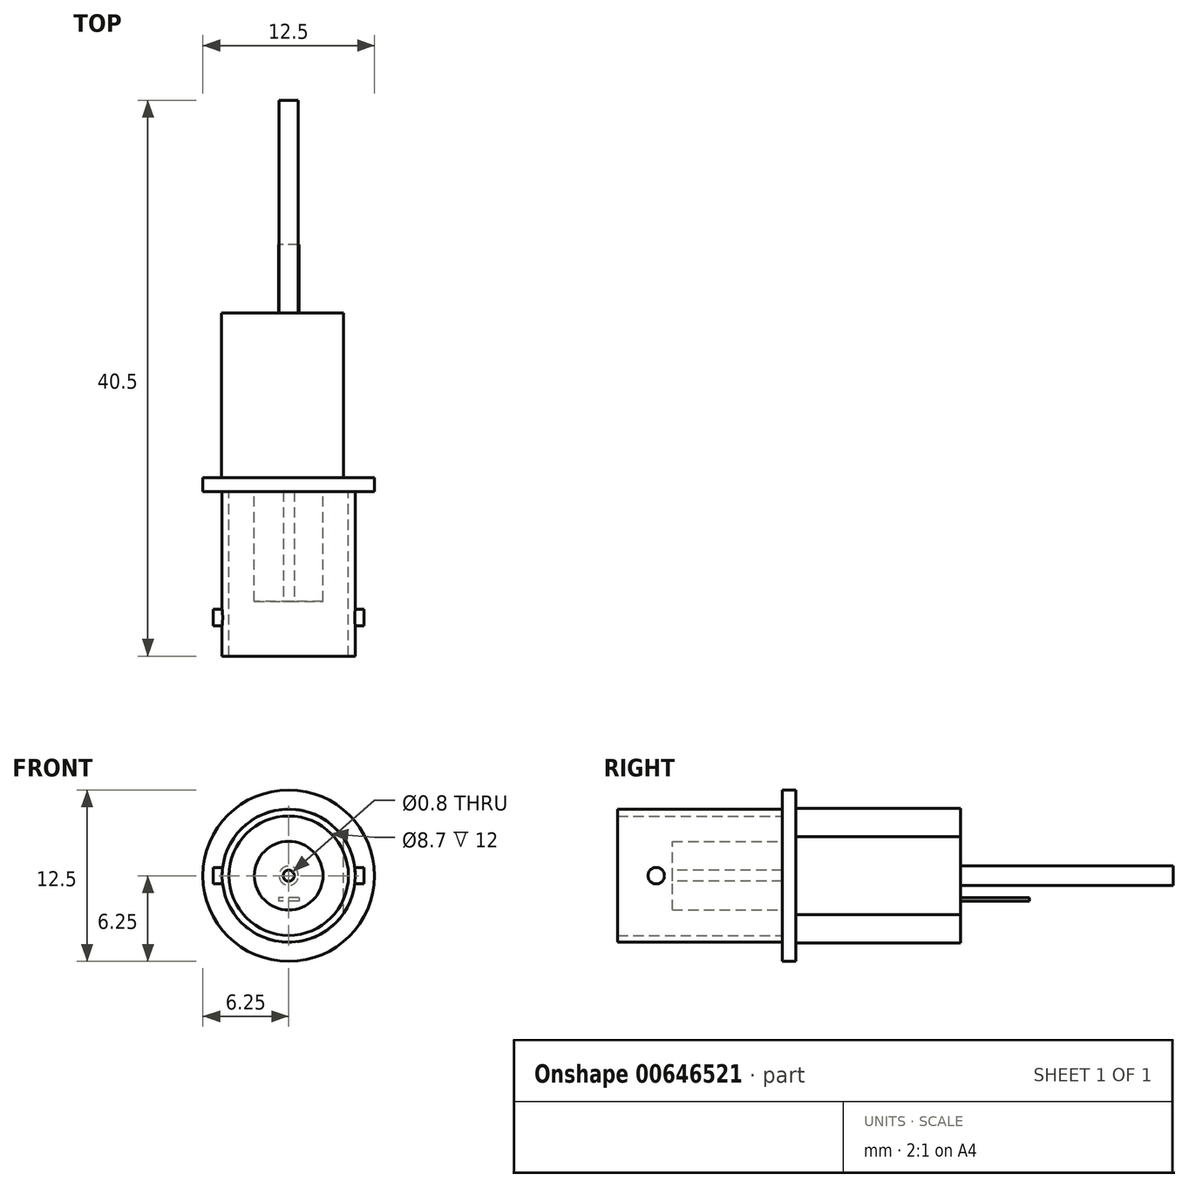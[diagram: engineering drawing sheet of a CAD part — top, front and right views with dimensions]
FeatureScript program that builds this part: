
annotation { "Feature Type Name" : "Feature", "Feature Type Description" : "" }
export const myFeature = defineFeature(function(context is Context, id is Id, definition is map)
    precondition{}
    {
        {
            var Q0;
            Q0=qCreatedBy(makeId("Front.planeOp"),FACE);
            var sketch = newSketch(context, id + "F0", { "sketchPlane" : qUnion([Q0])});
            skCircle(sketch, "E0", {"center": v(0, 0) * mm, "radius": 4.85 * mm});
            skCircle(sketch, "E1", {"center": v(0, 0) * mm, "radius": 4.35 * mm});
            skSolve(sketch);
        }
        {
            var Q0;
            Q0 = qSketchRegion(id + "F0", true);
            extrude(context, id + "F1", {"entities" : qUnion([Q0]), "depth" : 12 * mm, "offsetDistance" : 25 * mm});
        }
        {
            var Q0;
            Q0=qCreatedBy(makeId("Right.planeOp"),FACE);
            var sketch = newSketch(context, id + "F2", { "sketchPlane" : qUnion([Q0])});
            skCircle(sketch, "E2", {"center": v(-9.18, 0) * mm, "radius": 0.6 * mm});
            skSolve(sketch);
        }
        {
            var Q0;
            Q0 = qSketchRegion(id + "F2", true);
            extrude(context, id + "F3", {"entities" : qUnion([Q0]), "operationType" : NewBodyOperationType.ADD, "endBound" : BoundingType.SYMMETRIC, "depth" : 11 * mm, "offsetDistance" : 25 * mm});
        }
        {
            var Q0;
            Q0=qCreatedBy(makeId("Front.planeOp"),FACE);
            var sketch = newSketch(context, id + "F4", { "sketchPlane" : qUnion([Q0])});
            skCircle(sketch, "E3", {"center": v(0, 0) * mm, "radius": 4.35 * mm});
            skSolve(sketch);
        }
        {
            var Q0;
            Q0 = qSketchRegion(id + "F4", true);
            extrude(context, id + "F5", {"entities" : qUnion([Q0]), "operationType" : NewBodyOperationType.REMOVE, "depth" : 25 * mm, "offsetDistance" : 25 * mm});
        }
        {
            var Q0;
            Q0=qCreatedBy(makeId("Front.planeOp"),FACE);
            var sketch = newSketch(context, id + "F6", { "sketchPlane" : qUnion([Q0])});
            skCircle(sketch, "E4", {"center": v(0, 0) * mm, "radius": 2.5 * mm});
            skSolve(sketch);
        }
        {
            var Q0;
            Q0 = qSketchRegion(id + "F6", true);
            extrude(context, id + "F7", {"entities" : qUnion([Q0]), "depth" : 8 * mm, "offsetDistance" : 25 * mm});
        }
        {
            var Q0;
            Q0=makeQuery(id+"F7.opExtrude","CAP_FACE",FACE,{"disambiguationData":[OSD([sQuery(id+"F6.wireOp",EDGE,"E4")])],"isStart":false});
            var sketch = newSketch(context, id + "F8", { "sketchPlane" : qUnion([Q0])});
            skCircle(sketch, "E5", {"center": v(0, 0) * mm, "radius": 0.4 * mm});
            skSolve(sketch);
        }
        {
            var Q0;
            Q0 = qSketchRegion(id + "F8", true);
            extrude(context, id + "F9", {"entities" : qUnion([Q0]), "operationType" : NewBodyOperationType.REMOVE, "oppositeDirection" : true, "depth" : 25 * mm, "offsetDistance" : 25 * mm});
        }
        {
            var Q0;
            Q0=qCreatedBy(makeId("Front.planeOp"),FACE);
            var sketch = newSketch(context, id + "F10", { "sketchPlane" : qUnion([Q0])});
            skCircle(sketch, "E6", {"center": v(0, 0) * mm, "radius": 6.25 * mm});
            skSolve(sketch);
        }
        {
            var Q0;
            Q0 = qSketchRegion(id + "F10", true);
            extrude(context, id + "F11", {"entities" : qUnion([Q0]), "oppositeDirection" : true, "depth" : 1 * mm, "offsetDistance" : 25 * mm});
        }
        {
            var Q0;
            Q0=makeQuery(id+"F11.opExtrude","CAP_FACE",FACE,{"disambiguationData":[OSD([sQuery(id+"F10.wireOp",EDGE,"E6")])],"isStart":false});
            var sketch = newSketch(context, id + "F12", { "sketchPlane" : qUnion([Q0])});
            skCircle(sketch, "E7", {"center": v(0, 0) * mm, "radius": 4.9 * mm});
            skSolve(sketch);
        }
        {
            var Q0;
            Q0 = qSketchRegion(id + "F12", true);
            extrude(context, id + "F13", {"entities" : qUnion([Q0]), "operationType" : NewBodyOperationType.ADD, "depth" : 12 * mm, "offsetDistance" : 25 * mm});
        }
        {
            var Q0;
            Q0=makeQuery(id+"F13.opExtrude","CAP_FACE",FACE,{"disambiguationData":[OSD([sQuery(id+"F12.wireOp",EDGE,"E7")])],"isStart":false});
            var sketch = newSketch(context, id + "F14", { "sketchPlane" : qUnion([Q0])});
            skCircle(sketch, "E8", {"center": v(0, 0) * mm, "radius": 0.7 * mm});
            skSolve(sketch);
        }
        {
            var Q0;
            Q0 = qSketchRegion(id + "F14", true);
            extrude(context, id + "F15", {"entities" : qUnion([Q0]), "operationType" : NewBodyOperationType.ADD, "depth" : 15.5 * mm, "offsetDistance" : 25 * mm});
        }
        {
            var Q0;
            Q0=makeQuery(id+"F13.opExtrude","CAP_FACE",FACE,{"disambiguationData":[OSD([sQuery(id+"F12.wireOp",EDGE,"E7")])],"isStart":false});
            var sketch = newSketch(context, id + "F16", { "sketchPlane" : qUnion([Q0])});
            skLineSegment(sketch, "E9.bottom", {"start": v(-0.75, -1.6) * mm, "end": v(0.75, -1.6) * mm});
            skLineSegment(sketch, "E9.top", {"start": v(-0.75, -1.85) * mm, "end": v(0.75, -1.85) * mm});
            skLineSegment(sketch, "E9.left", {"start": v(-0.75, -1.6) * mm, "end": v(-0.75, -1.85) * mm});
            skLineSegment(sketch, "E9.right", {"start": v(0.75, -1.6) * mm, "end": v(0.75, -1.85) * mm});
            skSolve(sketch);
        }
        {
            var Q0;
            Q0 = qSketchRegion(id + "F16", true);
            extrude(context, id + "F17", {"entities" : qUnion([Q0]), "operationType" : NewBodyOperationType.ADD, "depth" : 5 * mm, "offsetDistance" : 25 * mm});
        }
        {
            var Q0;
            Q0=qCreatedBy(makeId("Top.planeOp"),FACE);
            var sketch = newSketch(context, id + "F18", { "sketchPlane" : qUnion([Q0])});
            skLineSegment(sketch, "E10.bottom", {"start": v(7.95, 15.42) * mm, "end": v(4, 15.42) * mm});
            skLineSegment(sketch, "E10.top", {"start": v(7.95, 1) * mm, "end": v(4, 1) * mm});
            skLineSegment(sketch, "E10.left", {"start": v(7.95, 15.42) * mm, "end": v(7.95, 1) * mm});
            skLineSegment(sketch, "E10.right", {"start": v(4, 15.42) * mm, "end": v(4, 1) * mm});
            skSolve(sketch);
        }
        {
            var Q0;
            Q0 = qSketchRegion(id + "F18", true);
            extrude(context, id + "F19", {"entities" : qUnion([Q0]), "operationType" : NewBodyOperationType.REMOVE, "endBound" : BoundingType.SYMMETRIC, "oppositeDirection" : true, "depth" : 25 * mm, "offsetDistance" : 25 * mm});
        }
    });
